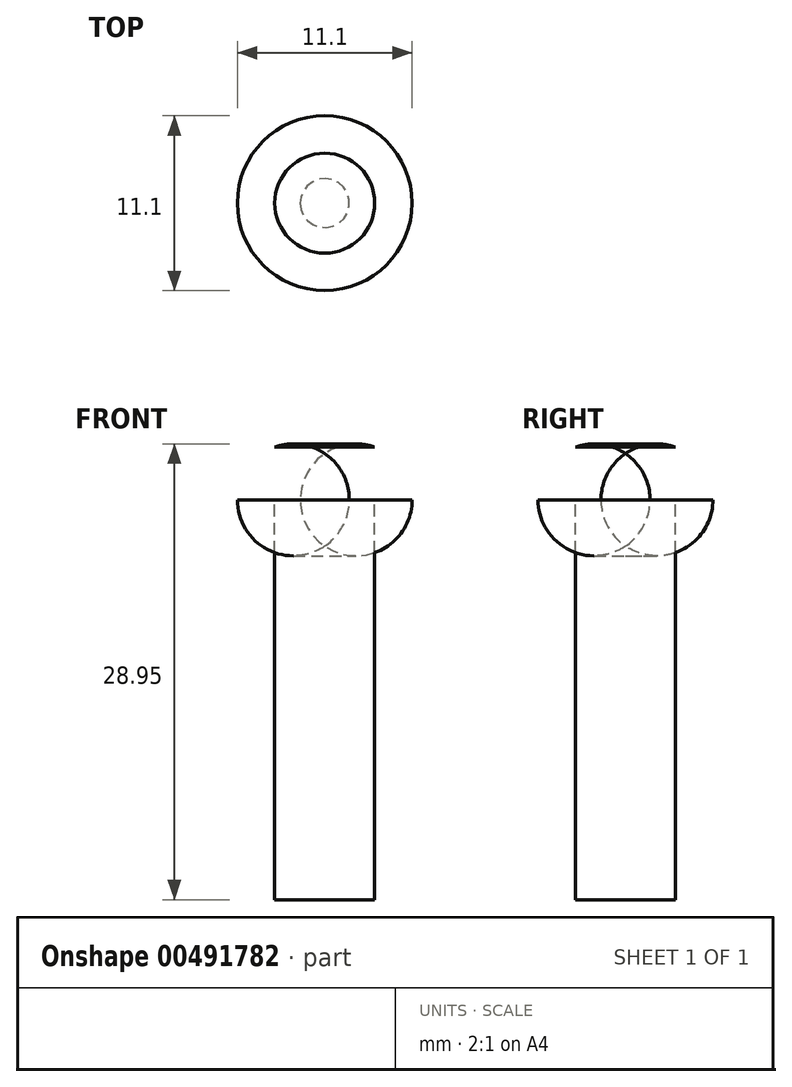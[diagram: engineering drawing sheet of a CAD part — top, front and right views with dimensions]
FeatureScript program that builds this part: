
annotation { "Feature Type Name" : "Feature", "Feature Type Description" : "" }
export const myFeature = defineFeature(function(context is Context, id is Id, definition is map)
    precondition{}
    {
        {
            var Q0;
            Q0=qCreatedBy(makeId("Top.planeOp"),FACE);
            var sketch = newSketch(context, id + "F0", { "sketchPlane" : qUnion([Q0])});
            skCircle(sketch, "E0", {"center": v(0, 0) * mm, "radius": 3.18 * mm});
            skSolve(sketch);
        }
        {
            var Q0;
            Q0=makeQuery(id+"F0.imprint","IMPRINT",FACE,{"disambiguationData":[TD([[makeQuery(id+"F0.imprint","IMPRINT",EDGE,{"derivedFrom":sQuery(id+"F0.wireOp",EDGE,"E0")}),1.0]])]});
            var Q1;
            Q1=sQuery(id+"F0.wireOp",EDGE,"E0");
            extrude(context, id + "F1", {"entities" : qUnion([Q0]), "surfaceEntities" : qUnion([Q1]), "oppositeDirection" : true, "depth" : 25.4 * mm});
        }
        {
            var Q0;
            Q0=qCreatedBy(makeId("Front.planeOp"),FACE);
            var sketch = newSketch(context, id + "F2", { "sketchPlane" : qUnion([Q0])});
            skLineSegment(sketch, "E1", {"start": v(0, 0) * mm, "end": v(0, 3.35) * mm});
            skLineSegment(sketch, "E2", {"start": v(0, 0) * mm, "end": v(-5.55, 0) * mm});
            skLineSegment(sketch, "E3", {"start": v(0, 3.35) * mm, "end": v(-3.18, 3.35) * mm});
            skArc(sketch, "E4", {"start": v(-3.18, 3.35) * mm, "mid": v(-4.9, 2.05) * mm, "end": v(-5.55, 0) * mm});
            skLineSegment(sketch, "E5", {"start": v(0, 0) * mm, "end": v(0, -25.4) * mm, "construction": true});
            skSolve(sketch);
        }
        {
            var Q0;
            Q0=makeQuery(id+"F2.imprint","IMPRINT",FACE,{"disambiguationData":[TD([[makeQuery(id+"F2.imprint","IMPRINT",EDGE,{"derivedFrom":sQuery(id+"F2.wireOp",EDGE,"E1")}),1.0]])]});
            var Q1;
            Q1=sQuery(id+"F2.wireOp",EDGE,"E5");
            revolve(context, id + "F3", {"operationType" : NewBodyOperationType.ADD, "entities" : qUnion([Q0]), "axis" : qUnion([Q1]), "revolveType" : RevolveType.FULL});
        }
    });
